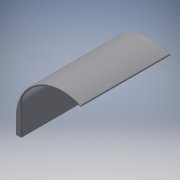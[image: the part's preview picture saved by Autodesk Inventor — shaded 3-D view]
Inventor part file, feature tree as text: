
AUTODESK INVENTOR PART (.ipt)
format: ipt  version: 2016 (Build 200138000, 138)  size: 190,464 bytes
history: native  units: mm
features: fillet x4, extrude x2, sketch x2, projected_geometry x1
ambient origin geometry x8: Origin, YZ Plane, XZ Plane, XY Plane, X Axis, Y Axis, Z Axis, Center Point
bodies: Solid1 (feature_tree)
feature tree (9):
  extrude  "Extrusion1"  Depth=120.0mm
  extrude  "Extrusion2"  Depth=2.0mm
  fillet  "Fillet1"  Radius=3.5mm
  fillet  "Fillet2"  Radius=4.0mm
  fillet  "Fillet3"  Radius=4.0mm
  fillet  "Fillet4"  Radius=4.0mm
  sketch  "Sketch1"  dims[d0=8.0mm d1=120.0mm]
  sketch  "Sketch2"  dims[d2=52.0mm d3=3.5mm d4=3.5mm d5=4.0mm d6=4.0mm d7=4.0mm d8=4.0mm d9=0.0mm d10=40.0mm d11=60.0mm d14=0.0mm d15=0.0mm d16=20.0mm d17=20.0mm d20=63.0mm d22=3.291209mm d23=1.5mm d24=2.0mm]
  projected_geometry  "Projected Loop1"
